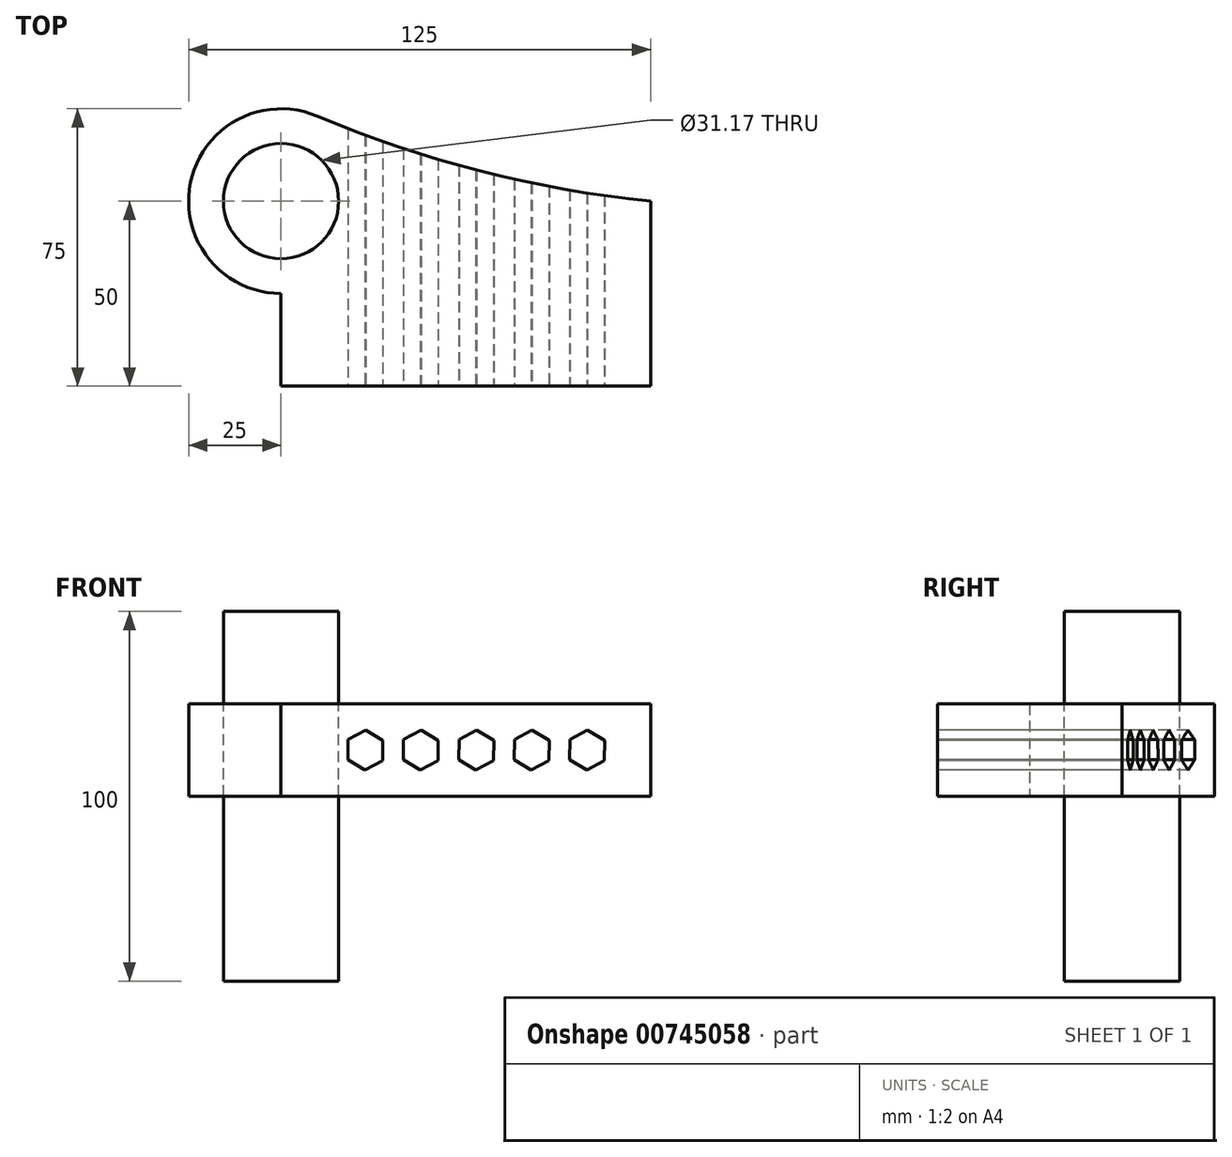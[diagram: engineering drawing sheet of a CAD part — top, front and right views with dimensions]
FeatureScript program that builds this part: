
annotation { "Feature Type Name" : "Feature", "Feature Type Description" : "" }
export const myFeature = defineFeature(function(context is Context, id is Id, definition is map)
    precondition{}
    {
        {
            var Q0;
            Q0=qCreatedBy(makeId("Top.planeOp"),FACE);
            var sketch = newSketch(context, id + "F0", { "sketchPlane" : qUnion([Q0])});
            skLineSegment(sketch, "E0.bottom", {"start": v(-50, 25) * mm, "end": v(50, 25) * mm});
            skLineSegment(sketch, "E0.top", {"start": v(-50, -25) * mm, "end": v(50, -25) * mm});
            skLineSegment(sketch, "E0.left", {"start": v(-50, 25) * mm, "end": v(-50, -25) * mm});
            skLineSegment(sketch, "E0.right", {"start": v(50, 25) * mm, "end": v(50, -25) * mm});
            skPoint(sketch, "E0.middle", {"position": v(0, 0) * mm});
            skCircle(sketch, "E1", {"center": v(-50, 25) * mm, "radius": 25 * mm});
            skArc(sketch, "E2", {"start": v(-40.27, 48.03) * mm, "mid": v(4, 33.13) * mm, "end": v(50, 25) * mm});
            skCircle(sketch, "E3", {"center": v(-50, 25) * mm, "radius": 15.59 * mm});
            skSolve(sketch);
        }
        {
            var Q0;
            Q0 = qSketchRegion(id + "F0", true);
            extrude(context, id + "F1", {"entities" : qUnion([Q0]), "depth" : 25 * mm, "offsetDistance" : 25 * mm});
        }
        {
            var Q0;
            {var subQ0=sQuery(id+"F0.wireOp",EDGE,"E0.left");var subQ1=sQuery(id+"F0.wireOp",EDGE,"E0.bottom");var subQ2=makeQuery(id+"F0.imprint","INTERSECT",VERTEX,{"derivedFrom":[subQ1,subQ0]});Q0=makeQuery(id+"F0.imprint","IMPRINT",FACE,{"disambiguationData":[TD([[makeQuery(id+"F0.imprint","IMPRINT",EDGE,{"disambiguationData":[TD([[subQ2,-1.0]])],"derivedFrom":subQ1}),1.0]])]});}
            var Q1;
            {var subQ0=sQuery(id+"F0.wireOp",EDGE,"E0.left");var subQ1=sQuery(id+"F0.wireOp",EDGE,"E0.bottom");var subQ2=makeQuery(id+"F0.imprint","INTERSECT",VERTEX,{"derivedFrom":[subQ1,subQ0]});Q1=makeQuery(id+"F0.imprint","IMPRINT",FACE,{"disambiguationData":[TD([[makeQuery(id+"F0.imprint","IMPRINT",EDGE,{"disambiguationData":[TD([[subQ2,-1.0]])],"derivedFrom":subQ1}),-1.0]])]});}
            extrude(context, id + "F2", {"entities" : qUnion([Q0, Q1]), "endBound" : BoundingType.SYMMETRIC, "oppositeDirection" : true, "depth" : 100 * mm, "offsetDistance" : 25 * mm});
        }
        {
            var Q0;
            Q0=makeQuery(id+"F1.opExtrude","SWEPT_FACE",FACE,{"disambiguationData":[OSD([sQuery(id+"F0.wireOp",EDGE,"E0.top")])]});
            var sketch = newSketch(context, id + "F3", { "sketchPlane" : qUnion([Q0])});
            skCircle(sketch, "E4.cCircle", {"center": v(-27.2, 12.5) * mm, "radius": 4.7 * mm, "construction": true});
            skPoint(sketch, "E4.cCircle.centerSnap0", {"position": v(-50, 12.5) * mm});
            skLineSegment(sketch, "E4.0", {"start": v(-22.55, 9.7) * mm, "end": v(-27.3, 7.08) * mm});
            skLineSegment(sketch, "E4.1", {"start": v(-27.3, 7.08) * mm, "end": v(-31.95, 9.88) * mm});
            skLineSegment(sketch, "E4.2", {"start": v(-31.95, 9.88) * mm, "end": v(-31.84, 15.3) * mm});
            skLineSegment(sketch, "E4.3", {"start": v(-31.84, 15.3) * mm, "end": v(-27.08, 17.92) * mm});
            skLineSegment(sketch, "E4.4", {"start": v(-27.08, 17.92) * mm, "end": v(-22.44, 15.12) * mm});
            skLineSegment(sketch, "E4.5", {"start": v(-22.44, 15.12) * mm, "end": v(-22.55, 9.7) * mm});
            skPoint(sketch, "E4.0.midPoint", {"position": v(-24.93, 8.38) * mm});
            skPoint(sketch, "E5.1.0.0", {"position": v(-35, 12.5) * mm});
            skPoint(sketch, "E5.1.0.1", {"position": v(-9.93, 8.38) * mm});
            skLineSegment(sketch, "E5.1.0.2", {"start": v(-7.44, 15.12) * mm, "end": v(-7.55, 9.7) * mm});
            skLineSegment(sketch, "E5.1.0.3", {"start": v(-12.08, 17.92) * mm, "end": v(-7.44, 15.12) * mm});
            skLineSegment(sketch, "E5.1.0.4", {"start": v(-16.84, 15.3) * mm, "end": v(-12.08, 17.92) * mm});
            skLineSegment(sketch, "E5.1.0.5", {"start": v(-16.95, 9.88) * mm, "end": v(-16.84, 15.3) * mm});
            skCircle(sketch, "E5.1.0.6", {"center": v(-12.2, 12.5) * mm, "radius": 4.7 * mm, "construction": true});
            skLineSegment(sketch, "E5.1.0.7", {"start": v(-7.55, 9.7) * mm, "end": v(-12.3, 7.08) * mm});
            skLineSegment(sketch, "E5.1.0.8", {"start": v(-12.3, 7.08) * mm, "end": v(-16.95, 9.88) * mm});
            skPoint(sketch, "E5.2.0.0", {"position": v(-20, 12.5) * mm});
            skPoint(sketch, "E5.2.0.1", {"position": v(5.07, 8.38) * mm});
            skLineSegment(sketch, "E5.2.0.2", {"start": v(7.56, 15.12) * mm, "end": v(7.45, 9.7) * mm});
            skLineSegment(sketch, "E5.2.0.3", {"start": v(2.92, 17.92) * mm, "end": v(7.56, 15.12) * mm});
            skLineSegment(sketch, "E5.2.0.4", {"start": v(-1.84, 15.3) * mm, "end": v(2.92, 17.92) * mm});
            skLineSegment(sketch, "E5.2.0.5", {"start": v(-1.95, 9.88) * mm, "end": v(-1.84, 15.3) * mm});
            skCircle(sketch, "E5.2.0.6", {"center": v(2.8, 12.5) * mm, "radius": 4.7 * mm, "construction": true});
            skLineSegment(sketch, "E5.2.0.7", {"start": v(7.45, 9.7) * mm, "end": v(2.7, 7.08) * mm});
            skLineSegment(sketch, "E5.2.0.8", {"start": v(2.7, 7.08) * mm, "end": v(-1.95, 9.88) * mm});
            skPoint(sketch, "E5.3.0.0", {"position": v(-5, 12.5) * mm});
            skPoint(sketch, "E5.3.0.1", {"position": v(20.07, 8.38) * mm});
            skLineSegment(sketch, "E5.3.0.2", {"start": v(22.56, 15.12) * mm, "end": v(22.45, 9.7) * mm});
            skLineSegment(sketch, "E5.3.0.3", {"start": v(17.92, 17.92) * mm, "end": v(22.56, 15.12) * mm});
            skLineSegment(sketch, "E5.3.0.4", {"start": v(13.16, 15.3) * mm, "end": v(17.92, 17.92) * mm});
            skLineSegment(sketch, "E5.3.0.5", {"start": v(13.05, 9.88) * mm, "end": v(13.16, 15.3) * mm});
            skCircle(sketch, "E5.3.0.6", {"center": v(17.8, 12.5) * mm, "radius": 4.7 * mm, "construction": true});
            skLineSegment(sketch, "E5.3.0.7", {"start": v(22.45, 9.7) * mm, "end": v(17.7, 7.08) * mm});
            skLineSegment(sketch, "E5.3.0.8", {"start": v(17.7, 7.08) * mm, "end": v(13.05, 9.88) * mm});
            skPoint(sketch, "E5.4.0.0", {"position": v(10, 12.5) * mm});
            skPoint(sketch, "E5.4.0.1", {"position": v(35.07, 8.38) * mm});
            skLineSegment(sketch, "E5.4.0.2", {"start": v(37.56, 15.12) * mm, "end": v(37.45, 9.7) * mm});
            skLineSegment(sketch, "E5.4.0.3", {"start": v(32.92, 17.92) * mm, "end": v(37.56, 15.12) * mm});
            skLineSegment(sketch, "E5.4.0.4", {"start": v(28.16, 15.3) * mm, "end": v(32.92, 17.92) * mm});
            skLineSegment(sketch, "E5.4.0.5", {"start": v(28.05, 9.88) * mm, "end": v(28.16, 15.3) * mm});
            skCircle(sketch, "E5.4.0.6", {"center": v(32.8, 12.5) * mm, "radius": 4.7 * mm, "construction": true});
            skLineSegment(sketch, "E5.4.0.7", {"start": v(37.45, 9.7) * mm, "end": v(32.7, 7.08) * mm});
            skLineSegment(sketch, "E5.4.0.8", {"start": v(32.7, 7.08) * mm, "end": v(28.05, 9.88) * mm});
            skLineSegment(sketch, "E5.direction1", {"start": v(-50, 12.5) * mm, "end": v(-35, 12.5) * mm, "construction": true});
            skSolve(sketch);
        }
        {
            var Q0;
            Q0 = qSketchRegion(id + "F3", true);
            extrude(context, id + "F4", {"entities" : qUnion([Q0]), "operationType" : NewBodyOperationType.REMOVE, "oppositeDirection" : true, "depth" : 100 * mm, "offsetDistance" : 25 * mm});
        }
    });
